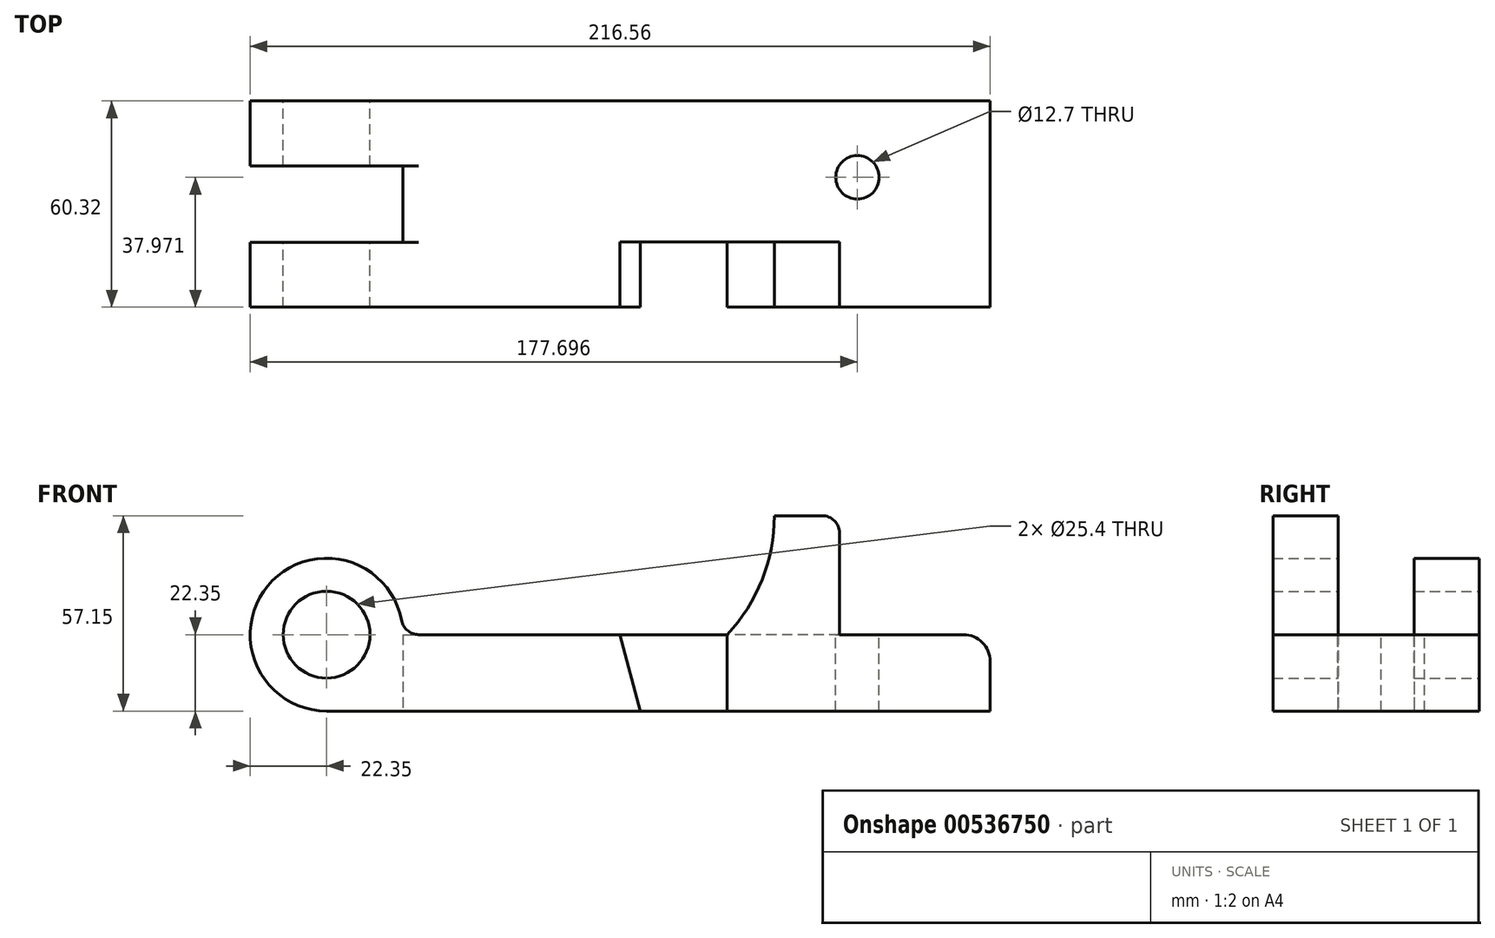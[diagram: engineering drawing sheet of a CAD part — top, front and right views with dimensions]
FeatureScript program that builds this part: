
annotation { "Feature Type Name" : "Feature", "Feature Type Description" : "" }
export const myFeature = defineFeature(function(context is Context, id is Id, definition is map)
    precondition{}
    {
        {
            var Q0;
            Q0=qCreatedBy(makeId("Front.planeOp"),FACE);
            var sketch = newSketch(context, id + "F0", { "sketchPlane" : qUnion([Q0])});
            skCircle(sketch, "E0", {"center": v(0, 0) * mm, "radius": 12.7 * mm});
            skCircle(sketch, "E1", {"center": v(0, 0) * mm, "radius": 22.35 * mm});
            skLineSegment(sketch, "E2", {"start": v(0, -22.35) * mm, "end": v(194.2, -22.35) * mm});
            skLineSegment(sketch, "E3", {"start": v(194.2, -22.35) * mm, "end": v(194.2, 0) * mm});
            skLineSegment(sketch, "E4", {"start": v(194.2, 0) * mm, "end": v(22.35, 0) * mm});
            skLineSegment(sketch, "E5", {"start": v(85.85, 0) * mm, "end": v(91.85, -22.35) * mm});
            skLineSegment(sketch, "E6", {"start": v(117.25, -22.35) * mm, "end": v(117.25, 0) * mm});
            skLineSegment(sketch, "E7", {"start": v(117.25, 0) * mm, "end": v(85.85, 0) * mm});
            skSolve(sketch);
        }
        {
            var Q0;
            Q0=makeQuery(id+"F0.imprint","IMPRINT",FACE,{"disambiguationData":[TD([[makeQuery(id+"F0.imprint","IMPRINT",EDGE,{"derivedFrom":sQuery(id+"F0.wireOp",EDGE,"E0")}),-1.0]])]});
            var Q1;
            {var subQ5=sQuery(id+"F0.wireOp",EDGE,"E5");Q1=makeQuery(id+"F0.imprint","IMPRINT",FACE,{"disambiguationData":[TD([[makeQuery(id+"F0.imprint","IMPRINT",EDGE,{"derivedFrom":subQ5}),-1.0]])]});}
            var Q2;
            {var subQ0=sQuery(id+"F0.wireOp",EDGE,"E3");Q2=makeQuery(id+"F0.imprint","IMPRINT",FACE,{"disambiguationData":[TD([[makeQuery(id+"F0.imprint","IMPRINT",EDGE,{"derivedFrom":subQ0}),1.0]])]});}
            var Q3;
            {var subQ0=sQuery(id+"F0.wireOp",EDGE,"E5");Q3=makeQuery(id+"F0.imprint","IMPRINT",FACE,{"disambiguationData":[TD([[makeQuery(id+"F0.imprint","IMPRINT",EDGE,{"derivedFrom":subQ0}),1.0]])]});}
            extrude(context, id + "F1", {"entities" : qUnion([Q0, Q1, Q2, Q3]), "endBound" : BoundingType.SYMMETRIC, "depth" : 60.32 * mm, "offsetDistance" : 25.4 * mm});
        }
        {
            var Q0;
            Q0=makeQuery(id+"F1.opExtrude","SWEPT_FACE",FACE,{"disambiguationData":[OSD([sQuery(id+"F0.wireOp",EDGE,"E4"),sQuery(id+"F0.wireOp",EDGE,"E7")])]});
            var sketch = newSketch(context, id + "F2", { "sketchPlane" : qUnion([Q0])});
            skLineSegment(sketch, "E8.bottom", {"start": v(22.35, -11.16) * mm, "end": v(-22.35, -11.16) * mm});
            skLineSegment(sketch, "E8.top", {"start": v(22.35, 11.16) * mm, "end": v(-22.35, 11.16) * mm});
            skLineSegment(sketch, "E8.left", {"start": v(22.35, -11.16) * mm, "end": v(22.35, 11.16) * mm});
            skLineSegment(sketch, "E8.right", {"start": v(-22.35, -11.16) * mm, "end": v(-22.35, 11.16) * mm});
            skPoint(sketch, "E8.middle", {"position": v(0, 0) * mm});
            skCircle(sketch, "E9", {"center": v(155.35, 7.81) * mm, "radius": 6.35 * mm});
            skSolve(sketch);
        }
        {
            var Q0;
            Q0=makeQuery(id+"F2.imprint","IMPRINT",FACE,{"disambiguationData":[TD([[makeQuery(id+"F2.imprint","IMPRINT",EDGE,{"derivedFrom":sQuery(id+"F2.wireOp",EDGE,"E8.bottom")}),-1.0]])]});
            extrude(context, id + "F3", {"entities" : qUnion([Q0]), "operationType" : NewBodyOperationType.REMOVE, "endBound" : BoundingType.THROUGH_ALL, "depth" : 25.4 * mm, "offsetDistance" : 25.4 * mm, "hasSecondDirection" : true, "secondDirectionBound" : SecondDirectionBoundingType.THROUGH_ALL, "secondDirectionOppositeDirection" : true, "secondDirectionDepth" : 25.4 * mm});
        }
        {
            var Q0;
            Q0=makeQuery(id+"F2.imprint","IMPRINT",FACE,{"disambiguationData":[TD([[makeQuery(id+"F2.imprint","IMPRINT",EDGE,{"derivedFrom":sQuery(id+"F2.wireOp",EDGE,"E9")}),1.0]])]});
            extrude(context, id + "F4", {"entities" : qUnion([Q0]), "operationType" : NewBodyOperationType.REMOVE, "endBound" : BoundingType.THROUGH_ALL, "oppositeDirection" : true, "depth" : 25.4 * mm, "offsetDistance" : 25.4 * mm});
        }
        {
            var Q0;
            Q0=makeQuery(id+"F1.opExtrude","CAP_FACE",FACE,{"disambiguationData":[OSD([sQuery(id+"F0.wireOp",EDGE,"E0"),sQuery(id+"F0.wireOp",EDGE,"E1"),sQuery(id+"F0.wireOp",EDGE,"E2"),sQuery(id+"F0.wireOp",EDGE,"E3"),sQuery(id+"F0.wireOp",EDGE,"E4"),sQuery(id+"F0.wireOp",EDGE,"E7")])],"isStart":false});
            var sketch = newSketch(context, id + "F5", { "sketchPlane" : qUnion([Q0])});
            skLineSegment(sketch, "E10.0", {"start": v(85.85, 0) * mm, "end": v(91.85, -22.35) * mm});
            skLineSegment(sketch, "E11.0", {"start": v(117.25, -22.35) * mm, "end": v(117.25, 0) * mm});
            skSolve(sketch);
        }
        {
            var Q0;
            {var subQ0=sQuery(id+"F5.wireOp",EDGE,"E10.0");Q0=makeQuery(id+"F5.imprint","IMPRINT",FACE,{"disambiguationData":[TD([[makeQuery(id+"F5.imprint","IMPRINT",EDGE,{"derivedFrom":subQ0}),1.0]])]});}
            extrude(context, id + "F6", {"entities" : qUnion([Q0]), "operationType" : NewBodyOperationType.REMOVE, "oppositeDirection" : true, "depth" : 19.05 * mm, "offsetDistance" : 25.4 * mm});
        }
        {
            var Q0;
            {var subQ0=sQuery(id+"F5.wireOp",EDGE,"E11.0");Q0=makeQuery(id+"F5.imprint","IMPRINT",FACE,{"disambiguationData":[TD([[makeQuery(id+"F5.imprint","IMPRINT",EDGE,{"derivedFrom":subQ0}),-1.0]])]});}
            var sketch = newSketch(context, id + "F7", { "sketchPlane" : qUnion([Q0])});
            skLineSegment(sketch, "E12", {"start": v(150.09, 0) * mm, "end": v(150.09, 34.8) * mm});
            skLineSegment(sketch, "E13", {"start": v(150.09, 34.8) * mm, "end": v(131.04, 34.8) * mm});
            skArc(sketch, "E14", {"start": v(117.25, 0) * mm, "mid": v(127.46, 16.08) * mm, "end": v(131.04, 34.8) * mm});
            skSolve(sketch);
        }
        {
            var Q0;
            {var subQ0=sQuery(id+"F7.wireOp",EDGE,"E12");Q0=makeQuery(id+"F7.imprint","IMPRINT",FACE,{"disambiguationData":[TD([[makeQuery(id+"F7.imprint","IMPRINT",EDGE,{"derivedFrom":subQ0}),1.0]])]});}
            extrude(context, id + "F8", {"entities" : qUnion([Q0]), "operationType" : NewBodyOperationType.ADD, "oppositeDirection" : true, "depth" : 19.05 * mm, "offsetDistance" : 25.4 * mm});
        }
        {
            var Q0;
            Q0=makeQuery(id+"F1.opExtrude","SWEPT_EDGE",EDGE,{"disambiguationData":[OSD([sQuery(id+"F0.wireOp",EDGE,"E3"),sQuery(id+"F0.wireOp",EDGE,"E4")])]});
            fillet(context, id + "F9", {"entities" : qUnion([Q0]), "radius" : 7.87 * mm, "tangentPropagation" : true, "allowEdgeOverflow" : false});
        }
        {
            var Q0;
            Q0=makeQuery(id+"F8.opExtrude","SWEPT_EDGE",EDGE,{"disambiguationData":[OSD([sQuery(id+"F7.wireOp",EDGE,"E12"),sQuery(id+"F7.wireOp",EDGE,"E13")])]});
            var Q1;
            Q1=makeQuery(id+"F8.opExtrude","SWEPT_EDGE",EDGE,{"disambiguationData":[OSD([sQuery(id+"F0.wireOp",EDGE,"E4"),sQuery(id+"F0.wireOp",EDGE,"E7"),sQuery(id+"F7.wireOp",EDGE,"E12")])]});
            var Q2;
            {var subQ0=sQuery(id+"F0.wireOp",EDGE,"E7");var subQ1=sQuery(id+"F0.wireOp",EDGE,"E4");var subQ2=makeQuery(id+"F1.opExtrude","SWEPT_FACE",FACE,{"disambiguationData":[OSD([subQ1,subQ0])]});var subQ3=sQuery(id+"F0.wireOp",EDGE,"E1");var subQ4=makeQuery(id+"F1.opExtrude","SWEPT_FACE",FACE,{"disambiguationData":[OSD([subQ3])]});Q2=makeQuery(id+"F3.boolean.opBoolean","SPLIT",EDGE,{"disambiguationData":[topologyDisambiguationEdgeConnected([subQ4,subQ2]),TD([makeQuery(id+"F3.opExtrude","SWEPT_FACE",FACE,{"disambiguationData":[OSD([sQuery(id+"F2.wireOp",EDGE,"E8.bottom")])]})])],"derivedFrom":makeQuery(id+"F1.opExtrude","SWEPT_EDGE",EDGE,{"disambiguationData":[OSD([subQ3,subQ1])]})});}
            var Q3;
            {var subQ0=sQuery(id+"F0.wireOp",EDGE,"E1");var subQ1=makeQuery(id+"F1.opExtrude","SWEPT_FACE",FACE,{"disambiguationData":[OSD([subQ0])]});var subQ2=sQuery(id+"F0.wireOp",EDGE,"E7");var subQ3=sQuery(id+"F0.wireOp",EDGE,"E4");var subQ4=makeQuery(id+"F1.opExtrude","SWEPT_FACE",FACE,{"disambiguationData":[OSD([subQ3,subQ2])]});Q3=makeQuery(id+"F3.boolean.opBoolean","SPLIT",EDGE,{"disambiguationData":[topologyDisambiguationEdgeConnected([subQ1,subQ4]),TD([makeQuery(id+"F3.opExtrude","SWEPT_FACE",FACE,{"disambiguationData":[OSD([sQuery(id+"F2.wireOp",EDGE,"E8.top")])]})])],"derivedFrom":makeQuery(id+"F1.opExtrude","SWEPT_EDGE",EDGE,{"disambiguationData":[OSD([subQ0,subQ3])]})});}
            fillet(context, id + "F10", {"entities" : qUnion([Q0, Q1, Q2, Q3]), "radius" : 5.08 * mm, "tangentPropagation" : true, "allowEdgeOverflow" : false});
        }
    });
